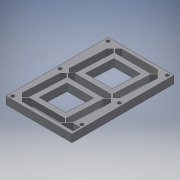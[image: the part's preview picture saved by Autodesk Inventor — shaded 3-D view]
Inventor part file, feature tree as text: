
AUTODESK INVENTOR PART (.ipt)
format: ipt  version: 2016 SP2 (Build 200236200, 236)  size: 487,424 bytes
history: native  units: mm
features: chamfer x8, extrude x4, sketch x3, reference x3, projected_geometry x2
ambient origin geometry x8: Origin, YZ Plane, XZ Plane, XY Plane, X Axis, Y Axis, Z Axis, Center Point
bodies: Volumenkörper1 (feature_tree)
feature tree (20):
  extrude  "Extrusion1"  TaperAngle=135.0deg  [1 undecoded]
  chamfer  "Fase3"  Distance=8.0mm
  chamfer  "Fase4"  Distance=10.5mm
  chamfer  "Fase5"  Distance=3.5mm
  chamfer  "Fase6"  Distance=3.5mm
  chamfer  "Fase7"  Distance=3.5mm
  chamfer  "Fase8"  Distance=3.5mm
  chamfer  "Fase9"  Distance=52.0mm
  chamfer  "Fase10"  Distance=1.0mm
  extrude  "Extrusion4"  Depth=5.0mm
  extrude  "Extrusion5"  Depth=10.5mm
  extrude  "Extrusion6"  Depth=10.5mm
  sketch  "Skizze1"  dims[d1=10.0mm d3=135.0deg]
  projected_geometry  "Projizierte Kontur1"
  sketch  "Skizze3"  dims[d6=5.0mm]
  sketch  "Skizze4"  dims[d9=0.523599mm d10=8.0mm d15=10.5mm d16=0.0mm d23=3.5mm d24=3.5mm d25=3.5mm d26=3.5mm d37=52.0mm d39=1.0mm d40=0.2mm d42=10.5mm d43=2.0mm d44=1.745329mm d45=10.5mm d46=2.0mm d47=1.745329mm d48=1.7mm d49=1.7mm d50=1.7mm d51=1.7mm d53=1.7mm d55=1.7mm d59=0.0mm d66=0.0mm d68=5.0mm d70=1.65mm d71=1.65mm d74=0.0mm d76=0.0mm d80=0.0mm d81=0.0mm d82=1.65mm d84=1.65mm d85=1.65mm d87=10.0mm d88=2.0mm d89=1.65mm d90=0.0mm d91=18.5mm d92=3.0mm d93=10.5mm d94=2.0mm d95=1.745329mm d96=10.5mm d97=2.0mm d98=1.745329mm d99=10.5mm d100=2.0mm d101=1.745329mm d102=10.5mm d103=2.0mm d104=1.745329mm d105=10.5mm d106=2.0mm d107=1.745329mm d108=10.5mm d109=2.0mm d110=1.745329mm d111=3.5mm d112=3.5mm d113=3.5mm d114=3.5mm d115=3.5mm d116=3.5mm d117=3.5mm d118=3.5mm d119=3.5mm d120=3.5mm d121=3.5mm d122=3.5mm d123=1.7mm d124=1.7mm d125=1.7mm d126=1.7mm d127=1.7mm d128=1.7mm d129=1.7mm d130=1.7mm d131=1.7mm d132=1.7mm d133=1.7mm d134=1.7mm d135=1.7mm d136=1.7mm d137=1.7mm d138=1.7mm d139=1.7mm d140=1.7mm d141=1.7mm d142=1.7mm d143=1.7mm d144=1.7mm d145=1.7mm d146=1.7mm d147=0.8mm d148=0.0mm d149=5.0mm d150=5.0mm d151=5.0mm d152=5.0mm d153=5.0mm d154=5.0mm d155=5.0mm d156=5.0mm d157=5.0mm d158=5.0mm d159=5.0mm d160=5.0mm d161=5.0mm d162=0.0mm d163=0.0mm d164=3.0mm d165=0.0mm d166=3.0mm d167=0.0mm d168=8.0mm d169=8.0mm d170=8.0mm d171=8.0mm d172=8.0mm d173=8.0mm d174=8.0mm d175=8.0mm d176=5.0mm d177=5.0mm d178=5.0mm d179=5.0mm d180=5.0mm d183=8.0mm d184=4.0mm d185=5.0mm]
  projected_geometry  "Projizierte Kontur2"
  reference  "Referenz1"
  reference  "Referenz2"
  reference  "Referenz3"
note: 1 required parameter value undecoded (feature->parameter linkage not recoverable at this tier; creation-order binding heuristic only, values carry confidence <= 0.55)
